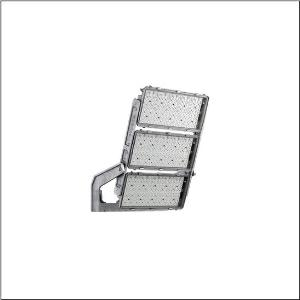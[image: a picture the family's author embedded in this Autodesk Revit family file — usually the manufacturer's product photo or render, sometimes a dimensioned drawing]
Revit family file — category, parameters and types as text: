
# Revit family: floodlight_fl_11_maxi_pro_remote___pl52_5xa779427d01aa_0793
name_source: partatom
category: Lighting Fixtures
units: mm (PartAtom-declared; Revit-internal decimal feet)

## family parameters
Cut with Voids When Loaded = No
Host = Face
Light Source = No
Part Type = Normal
Room Calculation Point = No
Round Connector Dimension = Use Diameter
Shared = No

## types (1)
- --- (1 x LED, 173640 lm, 1425.5 W, 5000K)
    Apparent Load = 1425 VA
    CIE Flux Codes = 24 55 98 100 100
    Color Rendering = 70
    Color Temperature = 5000K
    Default Elevation = 1800 mm
    Description = Floodlight FL 11  maxi  pro Remote floodlight; light control with lens of PMMA; cover panel of toughened safety glass, transparent; light distribution: PL52, asymmetric direct distribution, LEDcolour temperature: 5000K, rated luminous flux: 173.640lm, colour rendering: CRI > 70, light colour: 750; luminous efficacy: 122lm/W; brightness control: DALI 2 (1 DALI address); with terminal, 8-pole, max. 2.5mm², mains connection: 220..240V/380..400V AC, 50/60Hz, surge voltage resistance: line to ground: 10kV, ECG replaceable separately, LED unit replaceable without ESD environment, dustproof LED module, dimming range 10..100%, no afterglow with DALI off / DMX off command; 1426W floodlight with 3x LED unit of diecast aluminium, coated grey; length: 713mm / width: 651mm / height: 338mm; mounting bracket, of diecast aluminium, uncoated, natural, equipment: Power, protection rating (complete): IP66; insulation class (complete): insulation class I (protective earthing); certification: CE, ENEC, VDE; ball protection: ball impact resistance with accessories, impact resistance: IK07; rated ambient temperature 10°C, only for outdoor installations, permissible operating ambient temperature: -40..+30°C, permissible storage temperature: -40..+85°C; packaging unit: 1 piece

Light Distribution: PL52
    Height = 320 mm
    Lamp = 1 x LED
    Lamp Light Flux = 173640 lm
    Lamp Power = 1425.5 W
    Lamp count = 1
    Length = 1002 mm
    Luminous efficacy = 122 lm/W
    Manufacturer = Siteco
    ModVariant = No
    Model = 5XA779427D01AA
    Mounting Place = Ceiling
    Mounting Type = Surface mounted
    Number of Poles = 1
    OnlyDefault = Yes
    Power Factor = 1
    Product Name = Floodlight FL 11 maxi pro Remote | PL52
    Product group = floodlight | ceiling mounted
    ProductGroupID = 303
    Protection Class = Protection class I
    Protection Degree = IP 66
    RLX_Detail_Level = 1
    RLX_Emergency_Light_Flux = 0 lm
    RLX_Emergency_Type = 0
    RLX_Emergency_Type_DB = No
    RlxData = <blob elided: 52721 chars, md5=86074ccd>
    Socket = socket
    Standby Power = 0 W
    System Light Flux = 173640 lm
    System Power = 1425 W
    Type Comments = factory setting: luminous flux: 100 % | dim-lin: 254 | 980 mA
    Type Image = l_1006784.jpg
    URL = http://relux.com
    VarID = @adj_046433
    Voltage = 0 V
    Weight = 0.00 kg
    Width = 655 mm

## geometry (parser evidence)
native form markers: Blend x4, Sweep x12
no freeform markers — native parametric forms only
